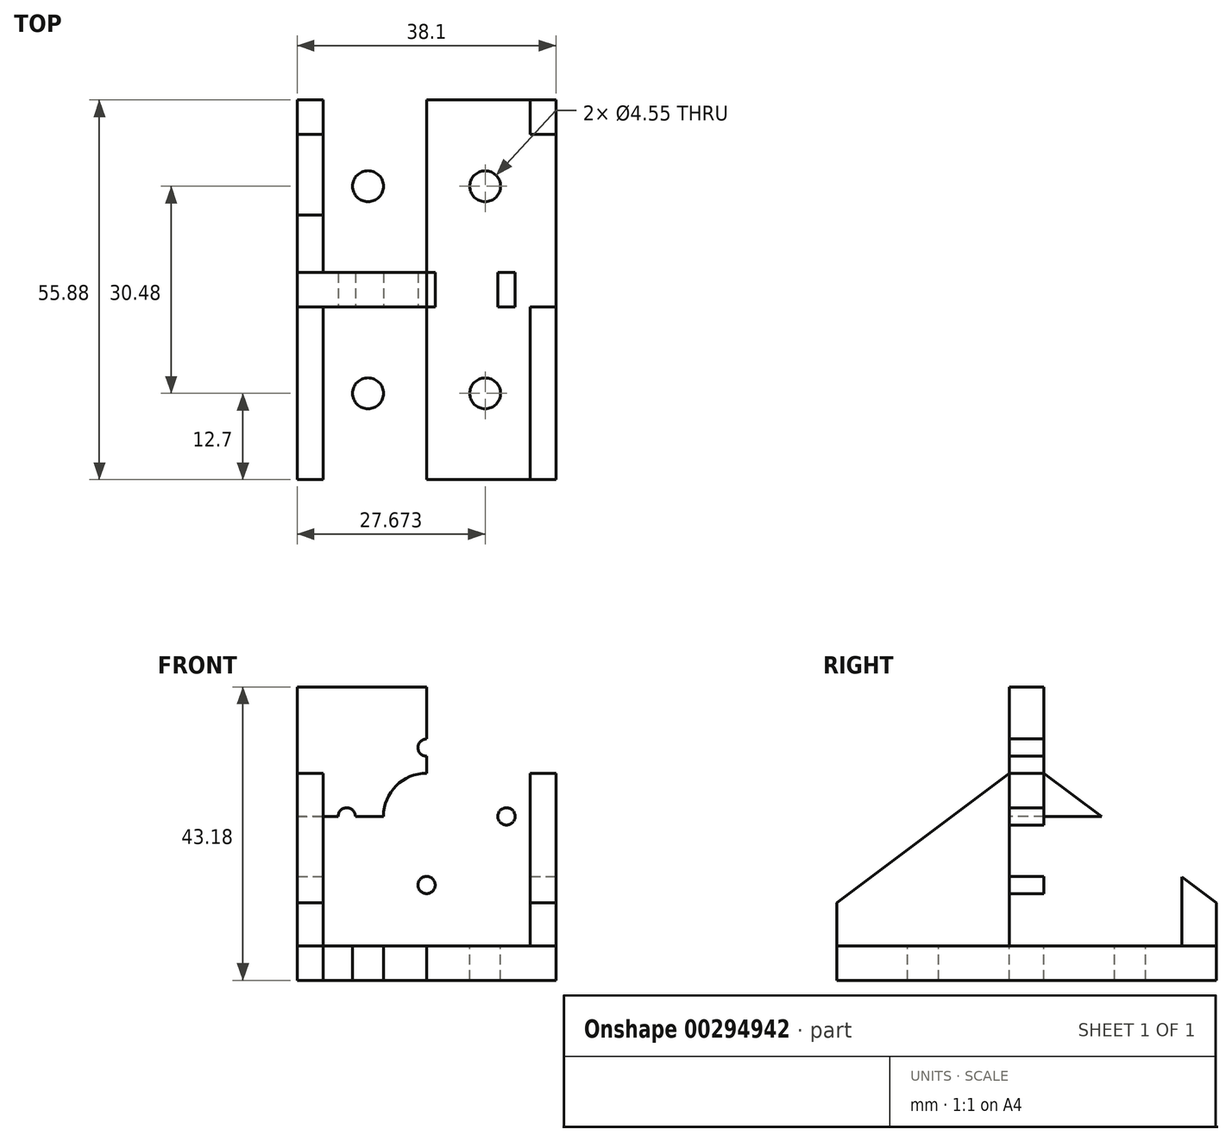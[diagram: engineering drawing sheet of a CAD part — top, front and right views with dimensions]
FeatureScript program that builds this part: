
annotation { "Feature Type Name" : "Feature", "Feature Type Description" : "" }
export const myFeature = defineFeature(function(context is Context, id is Id, definition is map)
    precondition{}
    {
        {
            var Q0;
            Q0=qCreatedBy(makeId("Top.planeOp"),FACE);
            var sketch = newSketch(context, id + "F0", { "sketchPlane" : qUnion([Q0])});
            skLineSegment(sketch, "E0.bottom", {"start": v(0, 0) * mm, "end": v(38.1, 0) * mm});
            skLineSegment(sketch, "E0.top", {"start": v(0, 55.88) * mm, "end": v(38.1, 55.88) * mm});
            skLineSegment(sketch, "E0.left", {"start": v(0, 0) * mm, "end": v(0, 55.88) * mm});
            skLineSegment(sketch, "E0.right", {"start": v(38.1, 0) * mm, "end": v(38.1, 55.88) * mm});
            skSolve(sketch);
        }
        {
            var Q0;
            Q0=qSketchRegion(id+"F0",true);
            extrude(context, id + "F1", {"entities" : qUnion([Q0]), "depth" : 5.08 * mm});
        }
        {
            var Q0;
            Q0=makeQuery(id+"F1.opExtrude","CAP_FACE",FACE,{"disambiguationData":[OSD([sQuery(id+"F0.wireOp",EDGE,"E0.bottom"),sQuery(id+"F0.wireOp",EDGE,"E0.top"),sQuery(id+"F0.wireOp",EDGE,"E0.left"),sQuery(id+"F0.wireOp",EDGE,"E0.right")])],"isStart":false});
            var sketch = newSketch(context, id + "F2", { "sketchPlane" : qUnion([Q0])});
            skLineSegment(sketch, "E1", {"start": v(0, 27.94) * mm, "end": v(38.1, 27.94) * mm});
            skLineSegment(sketch, "E2", {"start": v(0, 30.48) * mm, "end": v(38.1, 30.48) * mm});
            skLineSegment(sketch, "E3", {"start": v(0, 25.4) * mm, "end": v(38.1, 25.4) * mm});
            skSolve(sketch);
        }
        {
            var Q0;
            {var subQ0=sQuery(id+"F2.wireOp",EDGE,"E1");Q0=makeQuery(id+"F2.imprint","IMPRINT",FACE,{"disambiguationData":[TD([[makeQuery(id+"F2.imprint","IMPRINT",EDGE,{"derivedFrom":subQ0}),1.0]])]});}
            var Q1;
            {var subQ0=sQuery(id+"F2.wireOp",EDGE,"E1");Q1=makeQuery(id+"F2.imprint","IMPRINT",FACE,{"disambiguationData":[TD([[makeQuery(id+"F2.imprint","IMPRINT",EDGE,{"derivedFrom":subQ0}),-1.0]])]});}
            extrude(context, id + "F3", {"entities" : qUnion([Q0, Q1]), "operationType" : NewBodyOperationType.ADD, "depth" : 38.1 * mm});
        }
        {
            var Q0;
            Q0=makeQuery(id+"F3.opExtrude","SWEPT_FACE",FACE,{"disambiguationData":[OSD([sQuery(id+"F2.wireOp",EDGE,"E3")])]});
            var sketch = newSketch(context, id + "F4", { "sketchPlane" : qUnion([Q0])});
            skLineSegment(sketch, "E4.bottom", {"start": v(0, 43.18) * mm, "end": v(38.1, 43.18) * mm});
            skLineSegment(sketch, "E4.top", {"start": v(0, 5.08) * mm, "end": v(38.1, 5.08) * mm});
            skLineSegment(sketch, "E4.left", {"start": v(0, 43.18) * mm, "end": v(0, 5.08) * mm});
            skLineSegment(sketch, "E4.right", {"start": v(38.1, 43.18) * mm, "end": v(38.1, 5.08) * mm});
            skLineSegment(sketch, "E5", {"start": v(19.05, 43.18) * mm, "end": v(19.05, 5.08) * mm});
            skLineSegment(sketch, "E6", {"start": v(0, 24.13) * mm, "end": v(38.1, 24.13) * mm});
            skCircle(sketch, "E7", {"center": v(19.05, 24.13) * mm, "radius": 2.03 * mm});
            skCircle(sketch, "E8", {"center": v(30.81, 24.13) * mm, "radius": 1.27 * mm});
            skCircle(sketch, "E9", {"center": v(19.05, 34.24) * mm, "radius": 1.27 * mm});
            skCircle(sketch, "E10.MirrorC", {"center": v(7.29, 24.13) * mm, "radius": 1.27 * mm});
            skCircle(sketch, "E11.MirrorC", {"center": v(19.05, 14.02) * mm, "radius": 1.27 * mm});
            skCircle(sketch, "E12", {"center": v(19.05, 24.13) * mm, "radius": 6.35 * mm});
            skSolve(sketch);
        }
        {
            var Q0;
            {var subQ0=sQuery(id+"F0.wireOp",EDGE,"E0.left");var subQ1=sQuery(id+"F0.wireOp",EDGE,"E0.right");var subQ2=sQuery(id+"F0.wireOp",EDGE,"E0.bottom");Q0=makeQuery(id+"F3.boolean.opBoolean","SPLIT",FACE,{"disambiguationData":[TD([makeQuery(id+"F1.opExtrude","SWEPT_FACE",FACE,{"disambiguationData":[OSD([subQ2])]})])],"derivedFrom":makeQuery(id+"F1.opExtrude","CAP_FACE",FACE,{"disambiguationData":[OSD([subQ2,sQuery(id+"F0.wireOp",EDGE,"E0.top"),subQ0,subQ1])],"isStart":false})});}
            var sketch = newSketch(context, id + "F5", { "sketchPlane" : qUnion([Q0])});
            skLineSegment(sketch, "E13.bottom", {"start": v(0, 25.4) * mm, "end": v(38.1, 25.4) * mm});
            skLineSegment(sketch, "E13.top", {"start": v(0, 0) * mm, "end": v(38.1, 0) * mm});
            skLineSegment(sketch, "E13.left", {"start": v(0, 25.4) * mm, "end": v(0, 0) * mm});
            skLineSegment(sketch, "E13.right", {"start": v(38.1, 25.4) * mm, "end": v(38.1, 0) * mm});
            skLineSegment(sketch, "E14", {"start": v(19.05, 25.4) * mm, "end": v(19.05, 0) * mm});
            skLineSegment(sketch, "E15", {"start": v(3.8, 25.4) * mm, "end": v(3.81, 0) * mm});
            skLineSegment(sketch, "E16.MirrorCS", {"start": v(34.29, 25.4) * mm, "end": v(34.3, 0) * mm});
            skSolve(sketch);
        }
        {
            var Q0;
            {var subQ0=sQuery(id+"F5.wireOp",EDGE,"E13.left");Q0=makeQuery(id+"F5.imprint","IMPRINT",FACE,{"disambiguationData":[TD([[makeQuery(id+"F5.imprint","IMPRINT",EDGE,{"derivedFrom":subQ0}),-1.0]])]});}
            var Q1;
            {var subQ0=sQuery(id+"F5.wireOp",EDGE,"E13.right");Q1=makeQuery(id+"F5.imprint","IMPRINT",FACE,{"disambiguationData":[TD([[makeQuery(id+"F5.imprint","IMPRINT",EDGE,{"derivedFrom":subQ0}),1.0]])]});}
            extrude(context, id + "F6", {"entities" : qUnion([Q0, Q1]), "depth" : 38.1 * mm});
        }
        {
            var Q0;
            {var subQ0=sQuery(id+"F0.wireOp",EDGE,"E0.right");var subQ1=sQuery(id+"F0.wireOp",EDGE,"E0.left");var subQ2=sQuery(id+"F0.wireOp",EDGE,"E0.top");Q0=makeQuery(id+"F3.boolean.opBoolean","SPLIT",FACE,{"disambiguationData":[TD([makeQuery(id+"F1.opExtrude","SWEPT_FACE",FACE,{"disambiguationData":[OSD([subQ2])]})])],"derivedFrom":makeQuery(id+"F1.opExtrude","CAP_FACE",FACE,{"disambiguationData":[OSD([sQuery(id+"F0.wireOp",EDGE,"E0.bottom"),subQ2,subQ1,subQ0])],"isStart":false})});}
            var sketch = newSketch(context, id + "F7", { "sketchPlane" : qUnion([Q0])});
            skLineSegment(sketch, "E17.bottom", {"start": v(38.1, 30.48) * mm, "end": v(0, 30.48) * mm});
            skLineSegment(sketch, "E17.top", {"start": v(38.1, 55.88) * mm, "end": v(0, 55.88) * mm});
            skLineSegment(sketch, "E17.left", {"start": v(38.1, 30.48) * mm, "end": v(38.1, 55.88) * mm});
            skLineSegment(sketch, "E17.right", {"start": v(0, 30.48) * mm, "end": v(0, 55.88) * mm});
            skLineSegment(sketch, "E18", {"start": v(19.05, 30.48) * mm, "end": v(19.05, 55.88) * mm});
            skLineSegment(sketch, "E19", {"start": v(34.3, 30.48) * mm, "end": v(34.29, 55.88) * mm});
            skLineSegment(sketch, "E20.MirrorCS", {"start": v(3.8, 30.48) * mm, "end": v(3.81, 55.88) * mm});
            skSolve(sketch);
        }
        {
            var Q0;
            {var subQ0=sQuery(id+"F7.wireOp",EDGE,"E17.left");Q0=makeQuery(id+"F7.imprint","IMPRINT",FACE,{"disambiguationData":[TD([[makeQuery(id+"F7.imprint","IMPRINT",EDGE,{"derivedFrom":subQ0}),1.0]])]});}
            var Q1;
            {var subQ0=sQuery(id+"F7.wireOp",EDGE,"E17.right");Q1=makeQuery(id+"F7.imprint","IMPRINT",FACE,{"disambiguationData":[TD([[makeQuery(id+"F7.imprint","IMPRINT",EDGE,{"derivedFrom":subQ0}),-1.0]])]});}
            extrude(context, id + "F8", {"entities" : qUnion([Q0, Q1]), "depth" : 38.1 * mm});
        }
        {
            var Q0;
            Q0=makeQuery(id+"F8.opExtrude","SWEPT_FACE",FACE,{"disambiguationData":[OSD([sQuery(id+"F7.wireOp",EDGE,"E17.right")])]});
            var sketch = newSketch(context, id + "F9", { "sketchPlane" : qUnion([Q0])});
            skLineSegment(sketch, "E21", {"start": v(-55.88, 5.08) * mm, "end": v(-55.88, 11.43) * mm});
            skLineSegment(sketch, "E22", {"start": v(-30.48, 5.08) * mm, "end": v(-30.48, 30.48) * mm});
            skLineSegment(sketch, "E23", {"start": v(-55.88, 11.43) * mm, "end": v(-30.48, 30.48) * mm});
            skLineSegment(sketch, "E24", {"start": v(-27.94, 0) * mm, "end": v(-27.94, 51.6) * mm});
            skLineSegment(sketch, "E25.MirrorCS", {"start": v(0, 11.43) * mm, "end": v(-25.4, 30.48) * mm});
            skLineSegment(sketch, "E26.MirrorCS", {"start": v(-25.4, 5.08) * mm, "end": v(-25.4, 30.48) * mm});
            skLineSegment(sketch, "E27", {"start": v(-30.48, 5.08) * mm, "end": v(-55.88, 5.08) * mm});
            skLineSegment(sketch, "E28", {"start": v(-25.4, 5.08) * mm, "end": v(0, 5.08) * mm});
            skLineSegment(sketch, "E29", {"start": v(0, 11.43) * mm, "end": v(0, 5.08) * mm});
            skLineSegment(sketch, "E30.bottom", {"start": v(-55.88, 43.18) * mm, "end": v(-30.48, 43.18) * mm});
            skLineSegment(sketch, "E30.top", {"start": v(-55.88, 5.08) * mm, "end": v(-30.48, 5.08) * mm});
            skLineSegment(sketch, "E30.left", {"start": v(-55.88, 43.18) * mm, "end": v(-55.88, 5.08) * mm});
            skLineSegment(sketch, "E30.right", {"start": v(-30.48, 43.18) * mm, "end": v(-30.48, 5.08) * mm});
            skLineSegment(sketch, "E31.top", {"start": v(-25.4, 52) * mm, "end": v(0, 52) * mm});
            skLineSegment(sketch, "E31.left", {"start": v(-25.4, 5.08) * mm, "end": v(-25.4, 52) * mm});
            skLineSegment(sketch, "E31.right", {"start": v(0, 5.08) * mm, "end": v(0, 52) * mm});
            skSolve(sketch);
        }
        {
            var Q0;
            {var subQ0=sQuery(id+"F9.wireOp",EDGE,"E23");Q0=makeQuery(id+"F9.imprint","IMPRINT",FACE,{"disambiguationData":[TD([[makeQuery(id+"F9.imprint","IMPRINT",EDGE,{"derivedFrom":subQ0}),1.0]])]});}
            var Q1;
            {var subQ0=sQuery(id+"F9.wireOp",EDGE,"E25.MirrorCS");Q1=makeQuery(id+"F9.imprint","IMPRINT",FACE,{"disambiguationData":[TD([[makeQuery(id+"F9.imprint","IMPRINT",EDGE,{"derivedFrom":subQ0}),-1.0]])]});}
            extrude(context, id + "F10", {"entities" : qUnion([Q0, Q1]), "operationType" : NewBodyOperationType.REMOVE, "oppositeDirection" : true, "depth" : 127 * mm});
        }
        {
            var Q0;
            {var subQ0=sQuery(id+"F4.wireOp",EDGE,"E11.MirrorC");var subQ1=sQuery(id+"F4.wireOp",EDGE,"E5");var subQ2=makeQuery(id+"F4.imprint","INTERSECT",VERTEX,{"disambiguationData":[OD(0.0)],"derivedFrom":[subQ1,subQ0]});Q0=makeQuery(id+"F4.imprint","IMPRINT",FACE,{"disambiguationData":[TD([[makeQuery(id+"F4.imprint","IMPRINT",EDGE,{"disambiguationData":[TD([[subQ2,-1.0]])],"derivedFrom":subQ1}),-1.0]])]});}
            var Q1;
            {var subQ0=sQuery(id+"F4.wireOp",EDGE,"E11.MirrorC");var subQ1=sQuery(id+"F4.wireOp",EDGE,"E5");var subQ2=makeQuery(id+"F4.imprint","INTERSECT",VERTEX,{"disambiguationData":[OD(0.0)],"derivedFrom":[subQ1,subQ0]});Q1=makeQuery(id+"F4.imprint","IMPRINT",FACE,{"disambiguationData":[TD([[makeQuery(id+"F4.imprint","IMPRINT",EDGE,{"disambiguationData":[TD([[subQ2,-1.0]])],"derivedFrom":subQ1}),1.0]])]});}
            var Q2;
            {var subQ0=sQuery(id+"F4.wireOp",EDGE,"E8");var subQ1=sQuery(id+"F4.wireOp",EDGE,"E6");var subQ2=makeQuery(id+"F4.imprint","INTERSECT",VERTEX,{"disambiguationData":[OD(0.0)],"derivedFrom":[subQ1,subQ0]});Q2=makeQuery(id+"F4.imprint","IMPRINT",FACE,{"disambiguationData":[TD([[makeQuery(id+"F4.imprint","IMPRINT",EDGE,{"disambiguationData":[TD([[subQ2,-1.0]])],"derivedFrom":subQ1}),-1.0]])]});}
            var Q3;
            {var subQ0=sQuery(id+"F4.wireOp",EDGE,"E8");var subQ1=sQuery(id+"F4.wireOp",EDGE,"E6");var subQ2=makeQuery(id+"F4.imprint","INTERSECT",VERTEX,{"disambiguationData":[OD(0.0)],"derivedFrom":[subQ1,subQ0]});Q3=makeQuery(id+"F4.imprint","IMPRINT",FACE,{"disambiguationData":[TD([[makeQuery(id+"F4.imprint","IMPRINT",EDGE,{"disambiguationData":[TD([[subQ2,-1.0]])],"derivedFrom":subQ1}),1.0]])]});}
            var Q4;
            {var subQ0=sQuery(id+"F4.wireOp",EDGE,"E9");var subQ1=sQuery(id+"F4.wireOp",EDGE,"E5");var subQ2=makeQuery(id+"F4.imprint","INTERSECT",VERTEX,{"disambiguationData":[OD(0.0)],"derivedFrom":[subQ1,subQ0]});Q4=makeQuery(id+"F4.imprint","IMPRINT",FACE,{"disambiguationData":[TD([[makeQuery(id+"F4.imprint","IMPRINT",EDGE,{"disambiguationData":[TD([[subQ2,-1.0]])],"derivedFrom":subQ1}),1.0]])]});}
            var Q5;
            {var subQ0=sQuery(id+"F4.wireOp",EDGE,"E9");var subQ1=sQuery(id+"F4.wireOp",EDGE,"E5");var subQ2=makeQuery(id+"F4.imprint","INTERSECT",VERTEX,{"disambiguationData":[OD(0.0)],"derivedFrom":[subQ1,subQ0]});Q5=makeQuery(id+"F4.imprint","IMPRINT",FACE,{"disambiguationData":[TD([[makeQuery(id+"F4.imprint","IMPRINT",EDGE,{"disambiguationData":[TD([[subQ2,-1.0]])],"derivedFrom":subQ1}),-1.0]])]});}
            var Q6;
            {var subQ0=sQuery(id+"F4.wireOp",EDGE,"E10.MirrorC");var subQ1=sQuery(id+"F4.wireOp",EDGE,"E6");var subQ2=makeQuery(id+"F4.imprint","INTERSECT",VERTEX,{"disambiguationData":[OD(0.0)],"derivedFrom":[subQ1,subQ0]});Q6=makeQuery(id+"F4.imprint","IMPRINT",FACE,{"disambiguationData":[TD([[makeQuery(id+"F4.imprint","IMPRINT",EDGE,{"disambiguationData":[TD([[subQ2,-1.0]])],"derivedFrom":subQ1}),1.0]])]});}
            var Q7;
            {var subQ0=sQuery(id+"F4.wireOp",EDGE,"E10.MirrorC");var subQ1=sQuery(id+"F4.wireOp",EDGE,"E6");var subQ2=makeQuery(id+"F4.imprint","INTERSECT",VERTEX,{"disambiguationData":[OD(0.0)],"derivedFrom":[subQ1,subQ0]});Q7=makeQuery(id+"F4.imprint","IMPRINT",FACE,{"disambiguationData":[TD([[makeQuery(id+"F4.imprint","IMPRINT",EDGE,{"disambiguationData":[TD([[subQ2,-1.0]])],"derivedFrom":subQ1}),-1.0]])]});}
            extrude(context, id + "F11", {"entities" : qUnion([Q0, Q1, Q2, Q3, Q4, Q5, Q6, Q7]), "operationType" : NewBodyOperationType.REMOVE, "oppositeDirection" : true, "depth" : 25.4 * mm});
        }
        {
            var Q0;
            {var subQ0=sQuery(id+"F4.wireOp",EDGE,"E12");var subQ1=sQuery(id+"F4.wireOp",EDGE,"E5");var subQ2=makeQuery(id+"F4.imprint","INTERSECT",VERTEX,{"disambiguationData":[OD(0.0)],"derivedFrom":[subQ1,subQ0]});Q0=makeQuery(id+"F4.imprint","IMPRINT",FACE,{"disambiguationData":[TD([[makeQuery(id+"F4.imprint","IMPRINT",EDGE,{"disambiguationData":[TD([[subQ2,-1.0]])],"derivedFrom":subQ1}),-1.0]])]});}
            var Q1;
            {var subQ0=sQuery(id+"F4.wireOp",EDGE,"E12");var subQ1=sQuery(id+"F4.wireOp",EDGE,"E5");var subQ2=makeQuery(id+"F4.imprint","INTERSECT",VERTEX,{"disambiguationData":[OD(0.0)],"derivedFrom":[subQ1,subQ0]});Q1=makeQuery(id+"F4.imprint","IMPRINT",FACE,{"disambiguationData":[TD([[makeQuery(id+"F4.imprint","IMPRINT",EDGE,{"disambiguationData":[TD([[subQ2,-1.0]])],"derivedFrom":subQ1}),1.0]])]});}
            var Q2;
            {var subQ0=sQuery(id+"F4.wireOp",EDGE,"E7");var subQ1=sQuery(id+"F4.wireOp",EDGE,"E5");var subQ2=makeQuery(id+"F4.imprint","INTERSECT",VERTEX,{"disambiguationData":[OD(0.0)],"derivedFrom":[subQ1,subQ0]});Q2=makeQuery(id+"F4.imprint","IMPRINT",FACE,{"disambiguationData":[TD([[makeQuery(id+"F4.imprint","IMPRINT",EDGE,{"disambiguationData":[TD([[subQ2,-1.0]])],"derivedFrom":subQ1}),1.0]])]});}
            var Q3;
            {var subQ0=sQuery(id+"F4.wireOp",EDGE,"E7");var subQ1=sQuery(id+"F4.wireOp",EDGE,"E5");var subQ2=makeQuery(id+"F4.imprint","INTERSECT",VERTEX,{"disambiguationData":[OD(0.0)],"derivedFrom":[subQ1,subQ0]});Q3=makeQuery(id+"F4.imprint","IMPRINT",FACE,{"disambiguationData":[TD([[makeQuery(id+"F4.imprint","IMPRINT",EDGE,{"disambiguationData":[TD([[subQ2,-1.0]])],"derivedFrom":subQ1}),-1.0]])]});}
            var Q4;
            {var subQ0=sQuery(id+"F4.wireOp",EDGE,"E7");var subQ1=sQuery(id+"F4.wireOp",EDGE,"E5");var subQ2=makeQuery(id+"F4.imprint","INTERSECT",VERTEX,{"disambiguationData":[OD(1.0)],"derivedFrom":[subQ1,subQ0]});Q4=makeQuery(id+"F4.imprint","IMPRINT",FACE,{"disambiguationData":[TD([[makeQuery(id+"F4.imprint","IMPRINT",EDGE,{"disambiguationData":[TD([[subQ2,-1.0]])],"derivedFrom":subQ1}),-1.0]])]});}
            var Q5;
            {var subQ0=sQuery(id+"F4.wireOp",EDGE,"E6");var subQ1=sQuery(id+"F4.wireOp",EDGE,"E5");var subQ2=makeQuery(id+"F4.imprint","INTERSECT",VERTEX,{"derivedFrom":[subQ1,subQ0]});Q5=makeQuery(id+"F4.imprint","IMPRINT",FACE,{"disambiguationData":[TD([[makeQuery(id+"F4.imprint","IMPRINT",EDGE,{"disambiguationData":[TD([[subQ2,-1.0]])],"derivedFrom":subQ1}),-1.0]])]});}
            var Q6;
            {var subQ0=sQuery(id+"F4.wireOp",EDGE,"E6");var subQ1=sQuery(id+"F4.wireOp",EDGE,"E5");var subQ2=makeQuery(id+"F4.imprint","INTERSECT",VERTEX,{"derivedFrom":[subQ1,subQ0]});Q6=makeQuery(id+"F4.imprint","IMPRINT",FACE,{"disambiguationData":[TD([[makeQuery(id+"F4.imprint","IMPRINT",EDGE,{"disambiguationData":[TD([[subQ2,-1.0]])],"derivedFrom":subQ1}),1.0]])]});}
            var Q7;
            {var subQ0=sQuery(id+"F4.wireOp",EDGE,"E7");var subQ1=sQuery(id+"F4.wireOp",EDGE,"E5");var subQ2=makeQuery(id+"F4.imprint","INTERSECT",VERTEX,{"disambiguationData":[OD(1.0)],"derivedFrom":[subQ1,subQ0]});Q7=makeQuery(id+"F4.imprint","IMPRINT",FACE,{"disambiguationData":[TD([[makeQuery(id+"F4.imprint","IMPRINT",EDGE,{"disambiguationData":[TD([[subQ2,-1.0]])],"derivedFrom":subQ1}),1.0]])]});}
            extrude(context, id + "F12", {"entities" : qUnion([Q0, Q1, Q2, Q3, Q4, Q5, Q6, Q7]), "operationType" : NewBodyOperationType.REMOVE, "oppositeDirection" : true, "depth" : 25.4 * mm});
        }
        {
            var Q0;
            {var subQ0=sQuery(id+"F0.wireOp",EDGE,"E0.left");var subQ1=sQuery(id+"F0.wireOp",EDGE,"E0.right");var subQ2=sQuery(id+"F0.wireOp",EDGE,"E0.bottom");Q0=makeQuery(id+"F3.boolean.opBoolean","SPLIT",FACE,{"disambiguationData":[TD([makeQuery(id+"F1.opExtrude","SWEPT_FACE",FACE,{"disambiguationData":[OSD([subQ2])]})])],"derivedFrom":makeQuery(id+"F1.opExtrude","CAP_FACE",FACE,{"disambiguationData":[OSD([subQ2,sQuery(id+"F0.wireOp",EDGE,"E0.top"),subQ0,subQ1])],"isStart":false})});}
            var sketch = newSketch(context, id + "F13", { "sketchPlane" : qUnion([Q0])});
            skLineSegment(sketch, "E32.bottom", {"start": v(3.81, 25.4) * mm, "end": v(34.3, 25.4) * mm});
            skLineSegment(sketch, "E32.top", {"start": v(3.81, 0) * mm, "end": v(34.3, 0) * mm});
            skLineSegment(sketch, "E32.left", {"start": v(3.81, 25.4) * mm, "end": v(3.81, 0) * mm});
            skLineSegment(sketch, "E32.right", {"start": v(34.3, 25.4) * mm, "end": v(34.3, 0) * mm});
            skLineSegment(sketch, "E33", {"start": v(19.05, 25.4) * mm, "end": v(19.05, 0) * mm});
            skLineSegment(sketch, "E34", {"start": v(3.81, 12.7) * mm, "end": v(34.3, 12.7) * mm});
            skCircle(sketch, "E35", {"center": v(10.43, 12.7) * mm, "radius": 2.27 * mm});
            skCircle(sketch, "E36", {"center": v(27.67, 12.7) * mm, "radius": 2.27 * mm});
            skSolve(sketch);
        }
        {
            var Q0;
            {var subQ0=sQuery(id+"F13.wireOp",EDGE,"E35");var subQ1=sQuery(id+"F13.wireOp",EDGE,"E34");var subQ2=makeQuery(id+"F13.imprint","INTERSECT",VERTEX,{"disambiguationData":[OD(0.0)],"derivedFrom":[subQ1,subQ0]});Q0=makeQuery(id+"F13.imprint","IMPRINT",FACE,{"disambiguationData":[TD([[makeQuery(id+"F13.imprint","IMPRINT",EDGE,{"disambiguationData":[TD([[subQ2,-1.0]])],"derivedFrom":subQ1}),1.0]])]});}
            var Q1;
            {var subQ0=sQuery(id+"F13.wireOp",EDGE,"E35");var subQ1=sQuery(id+"F13.wireOp",EDGE,"E34");var subQ2=makeQuery(id+"F13.imprint","INTERSECT",VERTEX,{"disambiguationData":[OD(0.0)],"derivedFrom":[subQ1,subQ0]});Q1=makeQuery(id+"F13.imprint","IMPRINT",FACE,{"disambiguationData":[TD([[makeQuery(id+"F13.imprint","IMPRINT",EDGE,{"disambiguationData":[TD([[subQ2,-1.0]])],"derivedFrom":subQ1}),-1.0]])]});}
            var Q2;
            {var subQ0=sQuery(id+"F13.wireOp",EDGE,"E36");var subQ1=sQuery(id+"F13.wireOp",EDGE,"E34");var subQ2=makeQuery(id+"F13.imprint","INTERSECT",VERTEX,{"disambiguationData":[OD(0.0)],"derivedFrom":[subQ1,subQ0]});Q2=makeQuery(id+"F13.imprint","IMPRINT",FACE,{"disambiguationData":[TD([[makeQuery(id+"F13.imprint","IMPRINT",EDGE,{"disambiguationData":[TD([[subQ2,-1.0]])],"derivedFrom":subQ1}),1.0]])]});}
            var Q3;
            {var subQ0=sQuery(id+"F13.wireOp",EDGE,"E36");var subQ1=sQuery(id+"F13.wireOp",EDGE,"E34");var subQ2=makeQuery(id+"F13.imprint","INTERSECT",VERTEX,{"disambiguationData":[OD(0.0)],"derivedFrom":[subQ1,subQ0]});Q3=makeQuery(id+"F13.imprint","IMPRINT",FACE,{"disambiguationData":[TD([[makeQuery(id+"F13.imprint","IMPRINT",EDGE,{"disambiguationData":[TD([[subQ2,-1.0]])],"derivedFrom":subQ1}),-1.0]])]});}
            extrude(context, id + "F14", {"entities" : qUnion([Q0, Q1, Q2, Q3]), "operationType" : NewBodyOperationType.REMOVE, "oppositeDirection" : true, "depth" : 25.4 * mm});
        }
        {
            var Q0;
            {var subQ0=sQuery(id+"F0.wireOp",EDGE,"E0.right");var subQ1=sQuery(id+"F0.wireOp",EDGE,"E0.left");var subQ2=sQuery(id+"F0.wireOp",EDGE,"E0.top");Q0=makeQuery(id+"F3.boolean.opBoolean","SPLIT",FACE,{"disambiguationData":[TD([makeQuery(id+"F1.opExtrude","SWEPT_FACE",FACE,{"disambiguationData":[OSD([subQ2])]})])],"derivedFrom":makeQuery(id+"F1.opExtrude","CAP_FACE",FACE,{"disambiguationData":[OSD([sQuery(id+"F0.wireOp",EDGE,"E0.bottom"),subQ2,subQ1,subQ0])],"isStart":false})});}
            var sketch = newSketch(context, id + "F15", { "sketchPlane" : qUnion([Q0])});
            skLineSegment(sketch, "E37.bottom", {"start": v(3.81, 55.88) * mm, "end": v(34.29, 55.88) * mm});
            skLineSegment(sketch, "E37.top", {"start": v(3.81, 30.48) * mm, "end": v(34.29, 30.48) * mm});
            skLineSegment(sketch, "E37.left", {"start": v(3.81, 55.88) * mm, "end": v(3.81, 30.48) * mm});
            skLineSegment(sketch, "E37.right", {"start": v(34.29, 55.88) * mm, "end": v(34.29, 30.48) * mm});
            skLineSegment(sketch, "E38", {"start": v(19.05, 55.88) * mm, "end": v(19.05, 30.48) * mm});
            skLineSegment(sketch, "E39", {"start": v(3.81, 43.18) * mm, "end": v(34.29, 43.18) * mm});
            skCircle(sketch, "E40", {"center": v(10.43, 43.18) * mm, "radius": 2.27 * mm});
            skCircle(sketch, "E41", {"center": v(27.67, 43.18) * mm, "radius": 2.27 * mm});
            skSolve(sketch);
        }
        {
            var Q0;
            {var subQ0=sQuery(id+"F15.wireOp",EDGE,"E40");var subQ1=sQuery(id+"F15.wireOp",EDGE,"E39");var subQ2=makeQuery(id+"F15.imprint","INTERSECT",VERTEX,{"disambiguationData":[OD(0.0)],"derivedFrom":[subQ1,subQ0]});Q0=makeQuery(id+"F15.imprint","IMPRINT",FACE,{"disambiguationData":[TD([[makeQuery(id+"F15.imprint","IMPRINT",EDGE,{"disambiguationData":[TD([[subQ2,-1.0]])],"derivedFrom":subQ1}),1.0]])]});}
            var Q1;
            {var subQ0=sQuery(id+"F15.wireOp",EDGE,"E40");var subQ1=sQuery(id+"F15.wireOp",EDGE,"E39");var subQ2=makeQuery(id+"F15.imprint","INTERSECT",VERTEX,{"disambiguationData":[OD(0.0)],"derivedFrom":[subQ1,subQ0]});Q1=makeQuery(id+"F15.imprint","IMPRINT",FACE,{"disambiguationData":[TD([[makeQuery(id+"F15.imprint","IMPRINT",EDGE,{"disambiguationData":[TD([[subQ2,-1.0]])],"derivedFrom":subQ1}),-1.0]])]});}
            var Q2;
            {var subQ0=sQuery(id+"F15.wireOp",EDGE,"E41");var subQ1=sQuery(id+"F15.wireOp",EDGE,"E39");var subQ2=makeQuery(id+"F15.imprint","INTERSECT",VERTEX,{"disambiguationData":[OD(0.0)],"derivedFrom":[subQ1,subQ0]});Q2=makeQuery(id+"F15.imprint","IMPRINT",FACE,{"disambiguationData":[TD([[makeQuery(id+"F15.imprint","IMPRINT",EDGE,{"disambiguationData":[TD([[subQ2,-1.0]])],"derivedFrom":subQ1}),1.0]])]});}
            var Q3;
            {var subQ0=sQuery(id+"F15.wireOp",EDGE,"E41");var subQ1=sQuery(id+"F15.wireOp",EDGE,"E39");var subQ2=makeQuery(id+"F15.imprint","INTERSECT",VERTEX,{"disambiguationData":[OD(0.0)],"derivedFrom":[subQ1,subQ0]});Q3=makeQuery(id+"F15.imprint","IMPRINT",FACE,{"disambiguationData":[TD([[makeQuery(id+"F15.imprint","IMPRINT",EDGE,{"disambiguationData":[TD([[subQ2,-1.0]])],"derivedFrom":subQ1}),-1.0]])]});}
            extrude(context, id + "F16", {"entities" : qUnion([Q0, Q1, Q2, Q3]), "operationType" : NewBodyOperationType.REMOVE, "oppositeDirection" : true, "depth" : 25.4 * mm});
        }
    });
